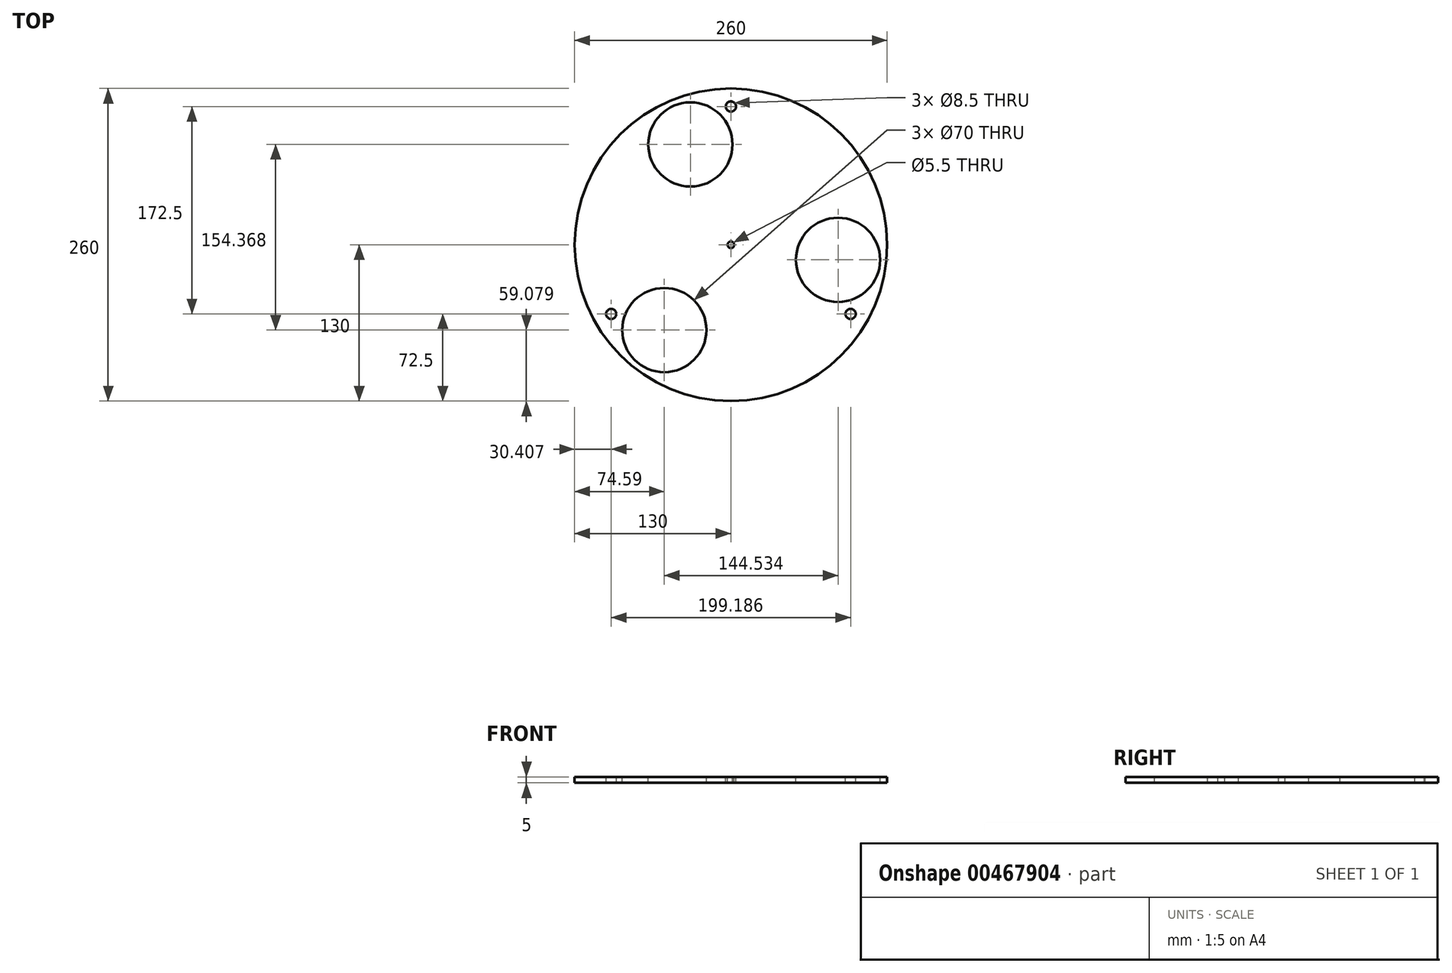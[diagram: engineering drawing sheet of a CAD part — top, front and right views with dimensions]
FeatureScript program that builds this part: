
annotation { "Feature Type Name" : "Feature", "Feature Type Description" : "" }
export const myFeature = defineFeature(function(context is Context, id is Id, definition is map)
    precondition{}
    {
        {
            var Q0;
            Q0=qCreatedBy(makeId("Top.planeOp"),FACE);
            var sketch = newSketch(context, id + "F0", { "sketchPlane" : qUnion([Q0])});
            skCircle(sketch, "E0", {"center": v(0, 0) * mm, "radius": 130 * mm});
            skSolve(sketch);
        }
        {
            var Q0;
            Q0=makeQuery(id+"F0.imprint","IMPRINT",FACE,{"disambiguationData":[TD([[makeQuery(id+"F0.imprint","IMPRINT",EDGE,{"derivedFrom":sQuery(id+"F0.wireOp",EDGE,"E0")}),1.0]])]});
            extrude(context, id + "F1", {"entities" : qUnion([Q0]), "depth" : 5 * mm});
        }
        {
            var Q0;
            Q0=makeQuery(id+"F1.opExtrude","CAP_FACE",FACE,{"disambiguationData":[OSD([sQuery(id+"F0.wireOp",EDGE,"E0")])],"isStart":false});
            var sketch = newSketch(context, id + "F2", { "sketchPlane" : qUnion([Q0])});
            skCircle(sketch, "E1", {"center": v(0, 0) * mm, "radius": 2.75 * mm});
            skCircle(sketch, "E2", {"center": v(0, 0) * mm, "radius": 115 * mm, "construction": true});
            skCircle(sketch, "E3", {"center": v(0, 115) * mm, "radius": 4.25 * mm});
            skLineSegment(sketch, "E4", {"start": v(0, 0) * mm, "end": v(-130.03, -75.07) * mm, "construction": true});
            skLineSegment(sketch, "E5", {"start": v(0, 0) * mm, "end": v(134.38, -77.59) * mm, "construction": true});
            skCircle(sketch, "E6", {"center": v(-99.6, -57.5) * mm, "radius": 4.25 * mm});
            skCircle(sketch, "E7", {"center": v(99.6, -57.5) * mm, "radius": 4.25 * mm});
            skSolve(sketch);
        }
        {
            var Q0;
            Q0=qSketchRegion(id+"F2",true);
            extrude(context, id + "F3", {"entities" : qUnion([Q0]), "operationType" : NewBodyOperationType.REMOVE, "endBound" : BoundingType.THROUGH_ALL, "oppositeDirection" : true, "depth" : 25 * mm});
        }
        {
            var Q0;
            Q0=makeQuery(id+"F1.opExtrude","CAP_FACE",FACE,{"disambiguationData":[OSD([sQuery(id+"F0.wireOp",EDGE,"E0")])],"isStart":false});
            var sketch = newSketch(context, id + "F4", { "sketchPlane" : qUnion([Q0])});
            skLineSegment(sketch, "E8", {"start": v(0, 0) * mm, "end": v(-33.71, 83.45) * mm, "construction": true});
            skCircle(sketch, "E9", {"center": v(-33.71, 83.45) * mm, "radius": 35 * mm});
            skCircle(sketch, "E10", {"center": v(0, 0) * mm, "radius": 45 * mm, "construction": true});
            skLineSegment(sketch, "E11", {"start": v(0, 0) * mm, "end": v(103.57, -14.56) * mm, "construction": true});
            skLineSegment(sketch, "E12", {"start": v(0, 0) * mm, "end": v(-61.88, -79.2) * mm, "construction": true});
            skCircle(sketch, "E13", {"center": v(89.12, -12.53) * mm, "radius": 35 * mm});
            skCircle(sketch, "E14", {"center": v(-55.4, -70.92) * mm, "radius": 35 * mm});
            skSolve(sketch);
        }
        {
            var Q0;
            Q0 = qSketchRegion(id + "F4", true);
            extrude(context, id + "F5", {"entities" : qUnion([Q0]), "operationType" : NewBodyOperationType.REMOVE, "endBound" : BoundingType.THROUGH_ALL, "oppositeDirection" : true, "depth" : 25 * mm});
        }
    });
